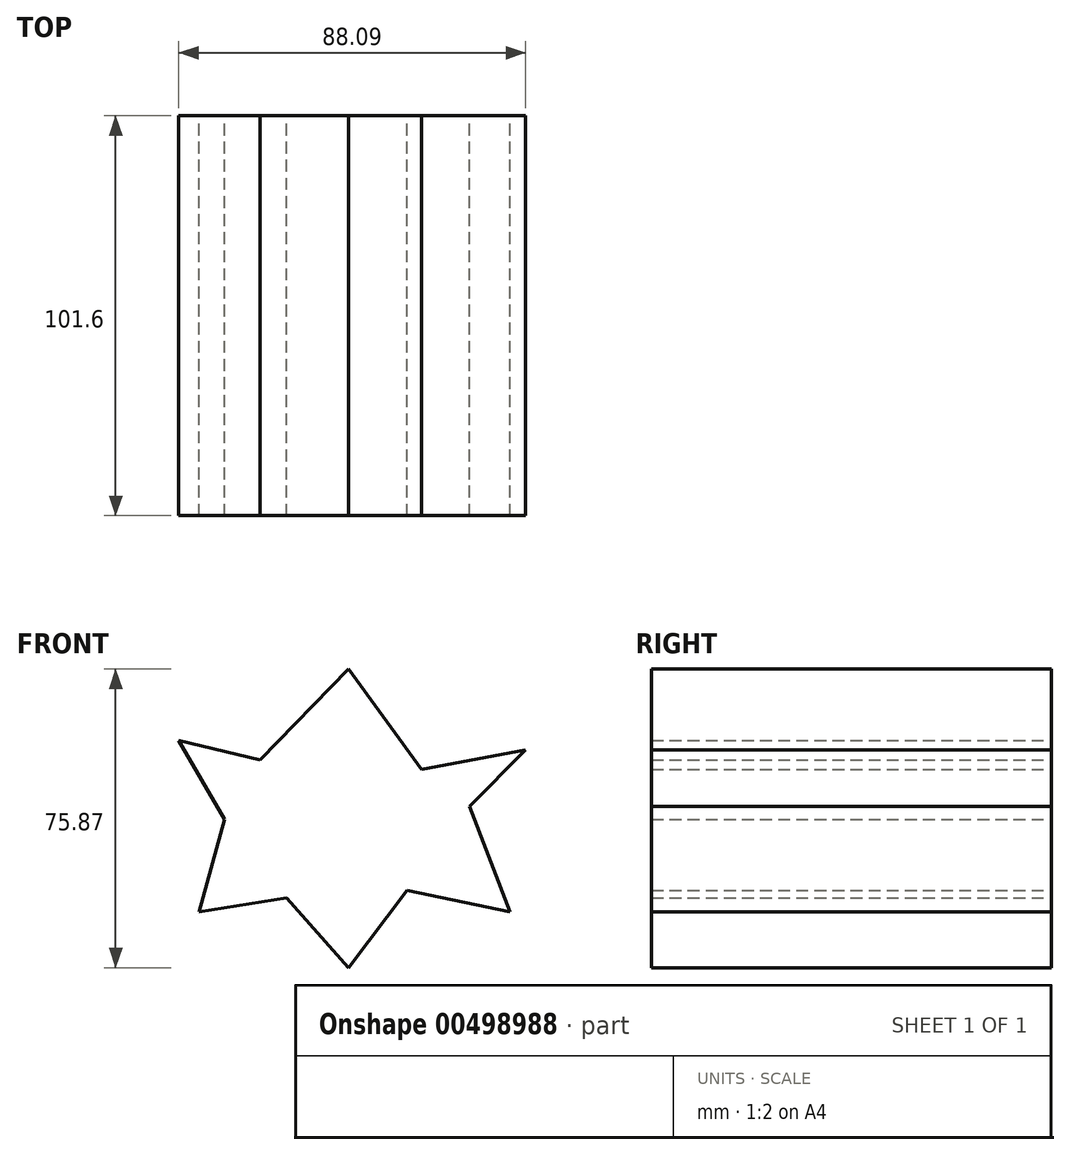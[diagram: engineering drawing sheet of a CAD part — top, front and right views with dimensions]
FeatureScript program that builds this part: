
annotation { "Feature Type Name" : "Feature", "Feature Type Description" : "" }
export const myFeature = defineFeature(function(context is Context, id is Id, definition is map)
    precondition{}
    {
        {
            var Q0;
            Q0=qCreatedBy(makeId("Front.planeOp"),FACE);
            var sketch = newSketch(context, id + "F0", { "sketchPlane" : qUnion([Q0])});
            skLineSegment(sketch, "E0", {"start": v(0, 0) * mm, "end": v(14.78, 19.7) * mm});
            skLineSegment(sketch, "E1", {"start": v(14.78, 19.7) * mm, "end": v(41, 14.19) * mm});
            skLineSegment(sketch, "E2", {"start": v(41, 14.19) * mm, "end": v(30.74, 41) * mm});
            skLineSegment(sketch, "E3", {"start": v(30.74, 41) * mm, "end": v(44.93, 55.38) * mm});
            skLineSegment(sketch, "E4", {"start": v(44.93, 55.38) * mm, "end": v(18.52, 50.45) * mm});
            skLineSegment(sketch, "E5", {"start": v(18.52, 50.45) * mm, "end": v(0, 75.87) * mm});
            skLineSegment(sketch, "E6", {"start": v(0, 75.87) * mm, "end": v(-22.47, 52.81) * mm});
            skLineSegment(sketch, "E7", {"start": v(-22.47, 52.81) * mm, "end": v(-43.16, 57.74) * mm});
            skLineSegment(sketch, "E8", {"start": v(-43.16, 57.74) * mm, "end": v(-31.53, 37.64) * mm});
            skLineSegment(sketch, "E9", {"start": v(-31.53, 37.64) * mm, "end": v(-38.03, 14.19) * mm});
            skLineSegment(sketch, "E10", {"start": v(-38.03, 14.19) * mm, "end": v(-15.77, 17.74) * mm});
            skLineSegment(sketch, "E11", {"start": v(-15.77, 17.74) * mm, "end": v(0, 0) * mm});
            skSolve(sketch);
        }
        {
            var Q0;
            Q0=makeQuery(id+"F0.imprint","IMPRINT",FACE,{"disambiguationData":[TD([[makeQuery(id+"F0.imprint","IMPRINT",EDGE,{"derivedFrom":sQuery(id+"F0.wireOp",EDGE,"E0")}),1.0]])]});
            extrude(context, id + "F1", {"entities" : qUnion([Q0]), "endBound" : BoundingType.SYMMETRIC, "depth" : 101.6 * mm, "offsetDistance" : 25.4 * mm});
        }
    });
